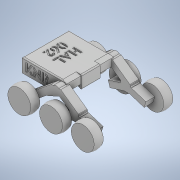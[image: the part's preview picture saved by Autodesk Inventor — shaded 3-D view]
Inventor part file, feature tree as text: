
AUTODESK INVENTOR PART (.ipt)
format: ipt  version: 2021 (Build 250183000, 183)  size: 4,547,584 bytes
history: native  units: mm
features: plane x4, sketch x4, split x3, extrude x3, revolve x1, pattern_linear x1, mirror x1, fillet x1
ambient origin geometry x8: Origin, YZ Plane, XZ Plane, XY Plane, X Axis, Y Axis, Z Axis, Center Point
bodies: Solid1 (feature_tree), Body7 (feature_tree)
feature tree (18):
  plane  "Work Plane1"
  split  "Split1"
  extrude  "Extrusion1"  Depth=10.0mm TaperAngle=0.0deg
  plane  "Work Plane4"
  split  "Split2"
  plane  "Work Plane5"
  revolve  "Revolution1"  [1 undecoded]
  pattern_linear  "Rectangular Pattern1"  Spacing1=90.0deg  [1 undecoded]
  plane  "Work Plane6"
  split  "Split3"
  mirror  "Mirror1"
  extrude  "Extrusion2"  Depth=1.4mm
  extrude  "Extrusion3"  Depth=1.4mm
  fillet  "Fillet2"  [1 undecoded]
  sketch  "Sketch1"  dims[d0=0.0mm d1=10.0mm d2=0.0mm]
  sketch  "Sketch4"  dims[d6=0.0mm d7=5.0mm]
  sketch  "Sketch5"  dims[d8=12.0mm]
  sketch  "Sketch6"  dims[d9=15.0mm d11=90.0deg d12=15.0mm d13=30.0mm d15=41.5mm d16=0.0mm d18=12.5mm d19=0.0mm d20=12.5mm d21=0.0mm d22=1.4mm]
note: 3 required parameter values undecoded (feature->parameter linkage not recoverable at this tier; creation-order binding heuristic only, values carry confidence <= 0.55)